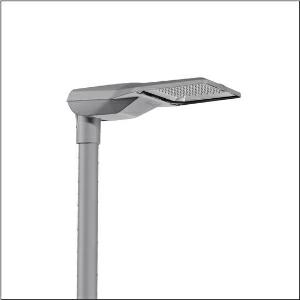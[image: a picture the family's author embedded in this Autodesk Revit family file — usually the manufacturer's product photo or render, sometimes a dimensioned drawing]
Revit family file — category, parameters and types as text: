
# Revit family: streetlight_sl_21_iq_midi___st1_0a_5xe3d41g08nb_8322
name_source: partatom
category: Lighting Fixtures
units: mm (PartAtom-declared; Revit-internal decimal feet)

## family parameters
Cut with Voids When Loaded = No
Host = Face
Light Source = No
Part Type = Normal
Room Calculation Point = No
Round Connector Dimension = Use Diameter
Shared = No

## types (1)
- --- (1 x LED, 24250 lm, 155.5 W, 4000K)
    Apparent Load = 155 VA
    CIE Flux Codes = 40 73 97 100 100
    Color Rendering = 70
    Color Temperature = 4000K
    Default Elevation = 1800 mm
    Description = Streetlight SL 21 iQ midi, mast luminaire, primary light control with lens, of PMMA, primary optical cover: cover, of toughened safety glass, transparent, light distribution: ST1.0a, light emission: direct distribution, primary light characteristic: asymmetric, installation type: post-top, side-entry, LED, High Power LED, rated luminous flux: 24.250lm, luminous efficacy: 156lm/W, light colour: 740, colour temperature: 4000K, control: Street-Remote, Auto-Match, Temp-Guard, Lumen-Switch, Night-Set, Smart-Wire, Light-Fading, Desk-Remote (wireless, voltage-free reading and setting of iQ features in the workshop via application-optimized NFC function/RFID function), optimised constant luminous flux control (CLO 2.0), pre-setting: linear dimming characteristic, mains connection: 230..240V, AC, 50/60Hz, start of lifetime: 156W, end of service life: 162W, reduction: 69W, luminaire housing, of diecast aluminium, powder-coated, Siteco® metallic grey (DB 702S), corrosivity category C5 mid according to DIN EN ISO 12944, please order mast flange separately, inclination adjustable: 0°, 5°, 10°, 15°, sealing non-destructively replaceable, multi-level sealing system, length: 644mm, width: 335mm, height: 110mm, mast flange for spigot size: 42mm (side-entry): 5XC10008XM4, 60/48mm (side-entry/post-top): 5XC10108XM2, 76/60mm (side-entry/post-top): 5XC10108XM1, protection rating (complete): IP66, insulation class (complete): insulation class II (safety insulation), certification: CE, ENEC, ENEC+, VDE, impact resistance: IK09, permissible operating ambient temperature for outdoor applications: -40..+50°C, standard-compliant lighting for roads and squares, packaging unit: 1 piece

Light Distribution: ST1.0a
    Height = 111 mm
    Lamp = 1 x LED
    Lamp Light Flux = 24250 lm
    Lamp Power = 155.5 W
    Lamp count = 1
    Length = 644 mm
    Luminous efficacy = 156 lm/W
    Manufacturer = Siteco
    ModVariant = No
    Model = 5XE3D41G08NB
    Number of Poles = 1
    OnlyDefault = Yes
    Power Factor = 1
    Product Name = Streetlight SL 21 iQ midi | ST1.0a
    Product group = mast luminaire | pylon top
    ProductGroupID = 6100
    Protection Class = Protection class II
    Protection Degree = IP 66
    RLX_Detail_Level = 1
    RLX_Emergency_Light_Flux = 0 lm
    RLX_Emergency_Type = 0
    RLX_Emergency_Type_DB = No
    RlxData = <blob elided: 91129 chars, md5=0e8b6372>
    Socket = socket
    Standby Power = 0 W
    System Light Flux = 24250 lm
    System Power = 155 W
    Type Comments = factory setting: luminous flux: 100 % | dim-lin: 254 | 823 mA
    Type Image = l_1004298.jpg
    URL = http://relux.com
    VarID = @adj_141537
    Voltage = 0 V
    Weight = 0.00 kg
    Width = 336 mm

## geometry (parser evidence)
native form markers: Blend x4, Sweep x10
no freeform markers — native parametric forms only
